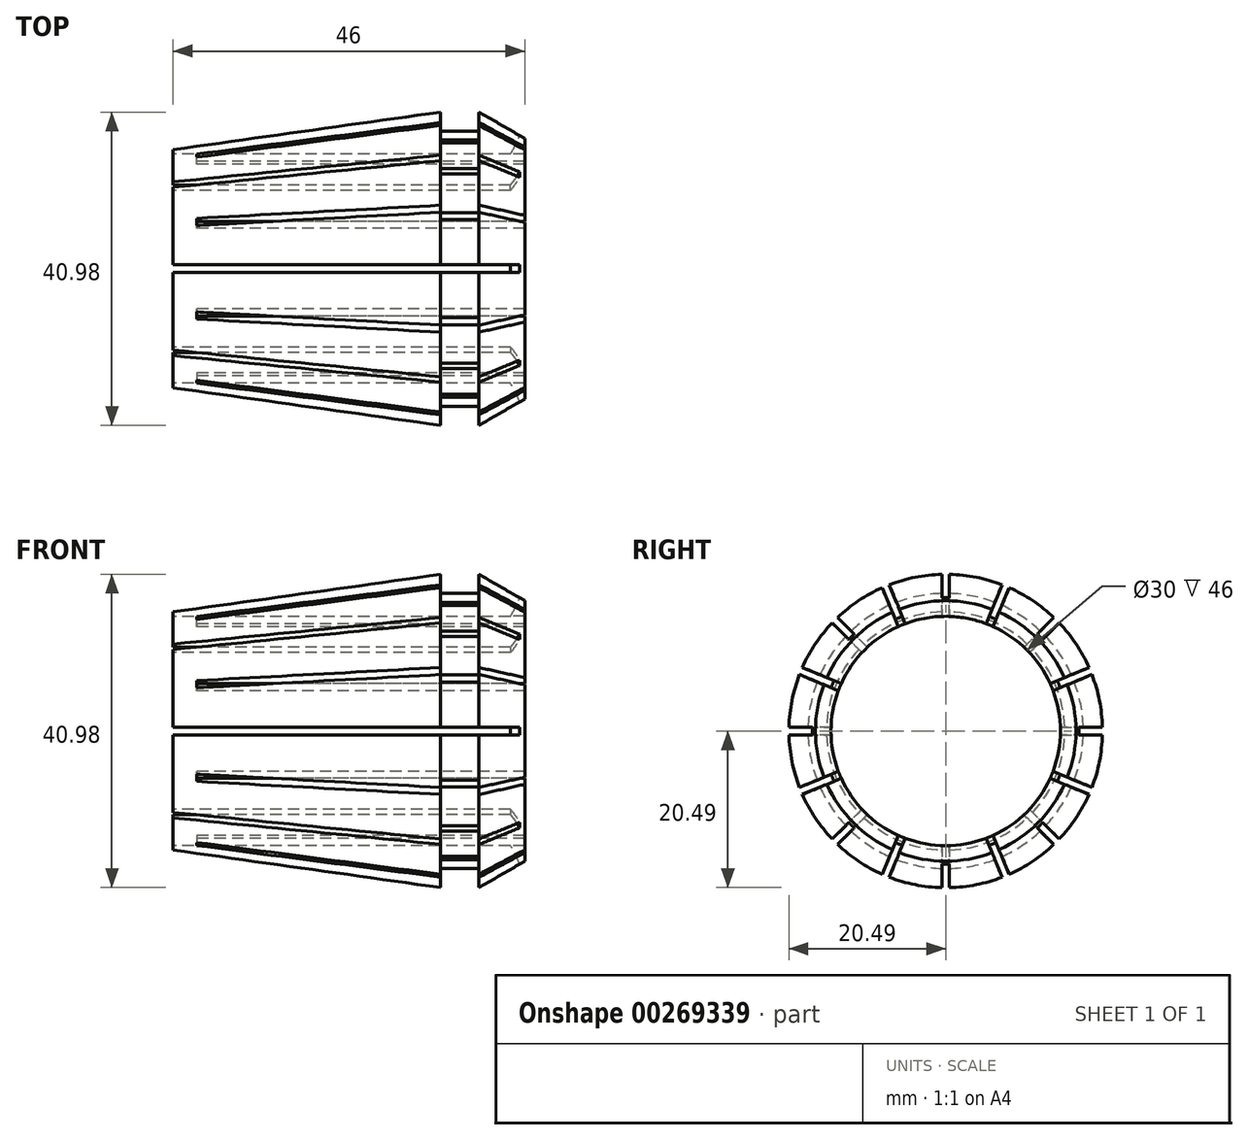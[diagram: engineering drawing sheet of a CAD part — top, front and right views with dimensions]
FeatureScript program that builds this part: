
annotation { "Feature Type Name" : "Feature", "Feature Type Description" : "" }
export const myFeature = defineFeature(function(context is Context, id is Id, definition is map)
    precondition{}
    {
        {
            var Q0;
            Q0=qCreatedBy(makeId("Front.planeOp"),FACE);
            var sketch = newSketch(context, id + "F0", { "sketchPlane" : qUnion([Q0])});
            skLineSegment(sketch, "E0.left", {"start": v(0, 15) * mm, "end": v(0, 15.58) * mm});
            skLineSegment(sketch, "E0.right", {"start": v(46, 15) * mm, "end": v(46, 17.04) * mm});
            skLineSegment(sketch, "E1", {"start": v(40, 20.5) * mm, "end": v(46, 17.04) * mm});
            skLineSegment(sketch, "E2", {"start": v(35, 20.5) * mm, "end": v(0, 15.58) * mm});
            skLineSegment(sketch, "E3", {"start": v(0, 15) * mm, "end": v(46, 15) * mm});
            skPoint(sketch, "E4.orphan", {"position": v(0, 0) * mm});
            skLineSegment(sketch, "E5", {"start": v(0, 0) * mm, "end": v(46, 0) * mm, "construction": true});
            skLineSegment(sketch, "E6", {"start": v(35, 20.5) * mm, "end": v(35, 18) * mm});
            skLineSegment(sketch, "E7", {"start": v(35, 18) * mm, "end": v(40, 18) * mm});
            skLineSegment(sketch, "E8", {"start": v(40, 18) * mm, "end": v(40, 20.5) * mm});
            skSolve(sketch);
        }
        {
            var Q0;
            Q0 = qSketchRegion(id + "F0", true);
            var Q1;
            Q1=sQuery(id+"F0.wireOp",EDGE,"E5");
            revolve(context, id + "F1", {"entities" : qUnion([Q0]), "axis" : qUnion([Q1]), "revolveType" : RevolveType.FULL});
        }
        {
            var Q0;
            Q0=qCreatedBy(makeId("Front.planeOp"),FACE);
            var sketch = newSketch(context, id + "F2", { "sketchPlane" : qUnion([Q0])});
            skLineSegment(sketch, "E9.bottom", {"start": v(0, 52.23) * mm, "end": v(46, 52.23) * mm});
            skLineSegment(sketch, "E9.top", {"start": v(0, 9.46) * mm, "end": v(34, 9.46) * mm});
            skLineSegment(sketch, "E9.left", {"start": v(0, 52.23) * mm, "end": v(0, 9.46) * mm});
            skLineSegment(sketch, "E9.right", {"start": v(46, 52.23) * mm, "end": v(46, 21.46) * mm});
            skPoint(sketch, "E10.visualSharp", {"position": v(46, 9.46) * mm});
            skArc(sketch, "E10.filletArc", {"start": v(34, 9.46) * mm, "mid": v(42.49, 12.98) * mm, "end": v(46, 21.46) * mm});
            skSolve(sketch);
        }
        {
            var Q0;
            Q0 = qSketchRegion(id + "F2", true);
            extrude(context, id + "F3", {"entities" : qUnion([Q0]), "depth" : 1 * mm, "symmetric" : true});
        }
        {
            var Q0;
            Q0=makeQuery(id+"F3.opExtrude","SWEPT_BODY",BODY,{"disambiguationData":[OSD([sQuery(id+"F2.wireOp",EDGE,"E9.bottom"),sQuery(id+"F2.wireOp",EDGE,"E9.top"),sQuery(id+"F2.wireOp",EDGE,"E9.left"),sQuery(id+"F2.wireOp",EDGE,"E9.right"),sQuery(id+"F2.wireOp",EDGE,"E10.filletArc")])]});
            var Q1;
            Q1=makeQuery(id+"F1.opRevolve","SWEPT_EDGE",EDGE,{"disambiguationData":[OSD([sQuery(id+"F0.wireOp",EDGE,"E1"),sQuery(id+"F0.wireOp",EDGE,"E8")])]});
            circularPattern(context, id + "F4", {"operationType" : NewBodyOperationType.REMOVE, "entities" : qUnion([Q0]), "axis" : qUnion([Q1]), "angle" : 360 * degree, "instanceCount" : 8, "equalSpace" : true});
        }
        {
            var Q0;
            Q0=qCreatedBy(makeId("Right.planeOp"),FACE);
            var sketch = newSketch(context, id + "F5", { "sketchPlane" : qUnion([Q0])});
            skLineSegment(sketch, "E11", {"start": v(0, 0) * mm, "end": v(-7.85, 18.94) * mm, "construction": true});
            skLineSegment(sketch, "E12", {"start": v(-7.85, 18.94) * mm, "end": v(0, 0) * mm, "construction": true});
            skSolve(sketch);
        }
        {
            var Q0;
            Q0=qCreatedBy(makeId("Top.planeOp"),FACE);
            var Q1;
            Q1=sQuery(id+"F5.wireOp",EDGE,"E11");
            cPlane(context, id + "F6", {"entities" : qUnion([Q0, Q1]), "cplaneType" : CPlaneType.LINE_ANGLE, "offset" : 25 * mm, "angle" : 0 * degree, "width" : 150 * mm, "height" : 150 * mm});
        }
        {
            var Q0;
            Q0=qCreatedBy(id+"F6.planeOp",FACE);
            var sketch = newSketch(context, id + "F7", { "sketchPlane" : qUnion([Q0])});
            skLineSegment(sketch, "E13.bottom", {"start": v(49.1, 0) * mm, "end": v(3.1, 0) * mm});
            skLineSegment(sketch, "E13.top", {"start": v(49.1, 22.26) * mm, "end": v(3.1, 22.26) * mm});
            skLineSegment(sketch, "E13.left", {"start": v(49.1, 0) * mm, "end": v(49.1, 22.26) * mm});
            skLineSegment(sketch, "E13.right", {"start": v(3.1, 0) * mm, "end": v(3.1, 22.26) * mm});
            skSolve(sketch);
        }
        {
            var Q0;
            Q0 = qSketchRegion(id + "F7", true);
            extrude(context, id + "F8", {"entities" : qUnion([Q0]), "depth" : 1 * mm, "symmetric" : true});
        }
        {
            var Q0;
            Q0=makeQuery(id+"F8.opExtrude","SWEPT_BODY",BODY,{"disambiguationData":[OSD([sQuery(id+"F7.wireOp",EDGE,"E13.bottom"),sQuery(id+"F7.wireOp",EDGE,"E13.top"),sQuery(id+"F7.wireOp",EDGE,"E13.left"),sQuery(id+"F7.wireOp",EDGE,"E13.right")])]});
            var Q1;
            Q1=makeQuery(id+"F1.opRevolve","SWEPT_FACE",FACE,{"disambiguationData":[OSD([sQuery(id+"F0.wireOp",EDGE,"E1")])]});
            circularPattern(context, id + "F9", {"operationType" : NewBodyOperationType.REMOVE, "entities" : qUnion([Q0]), "axis" : qUnion([Q1]), "angle" : 360 * degree, "instanceCount" : 8, "equalSpace" : true});
        }
    });
